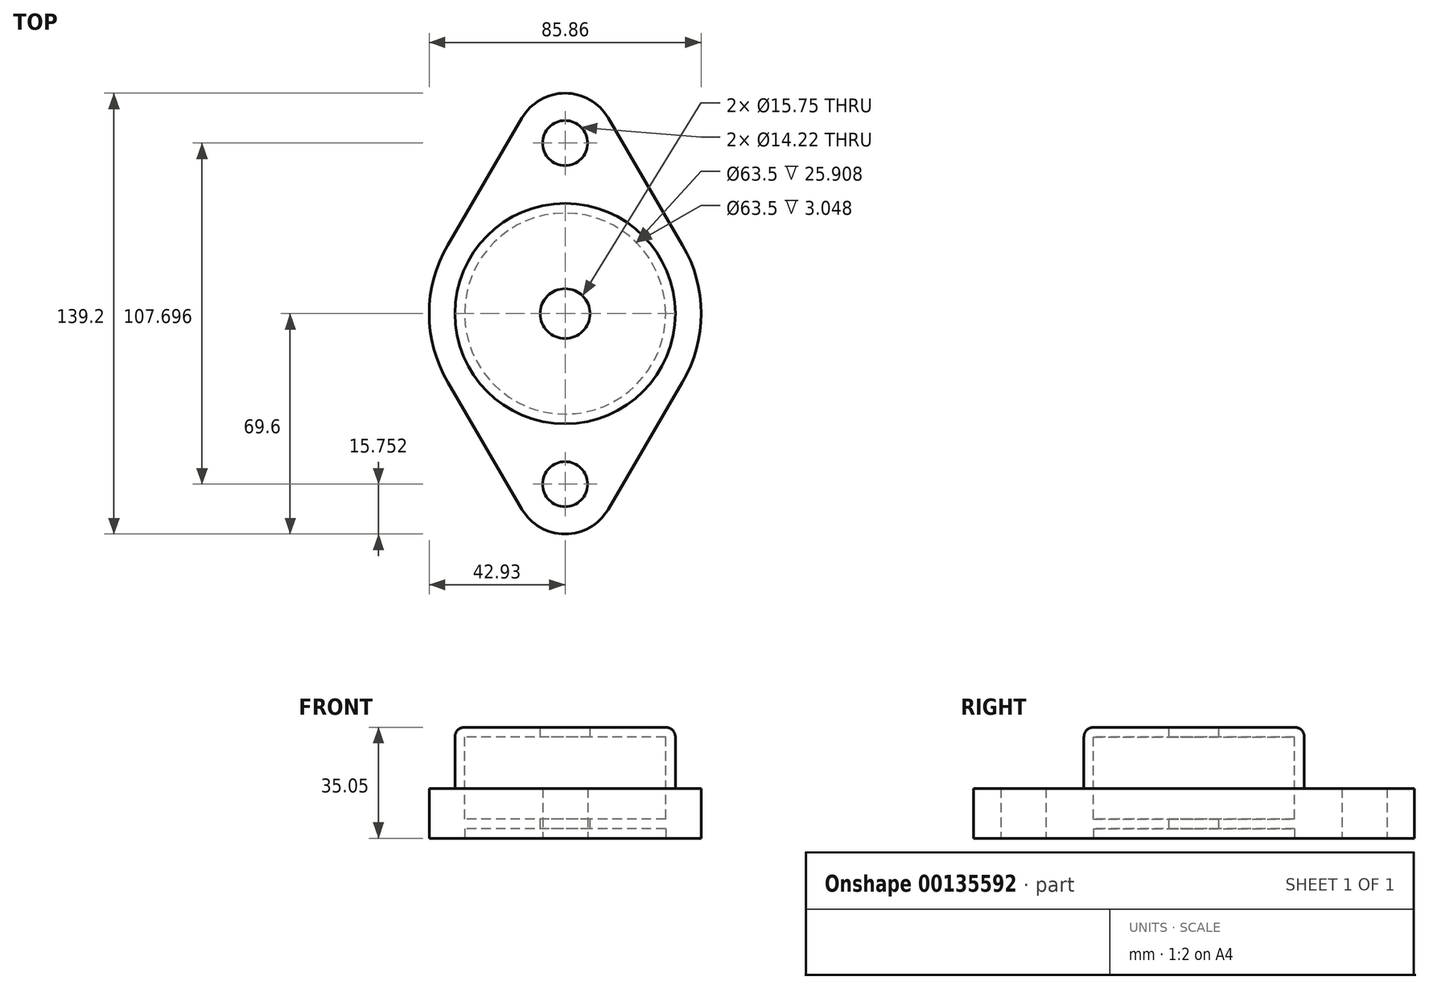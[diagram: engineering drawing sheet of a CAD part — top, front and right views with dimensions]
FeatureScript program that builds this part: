
annotation { "Feature Type Name" : "Feature", "Feature Type Description" : "" }
export const myFeature = defineFeature(function(context is Context, id is Id, definition is map)
    precondition{}
    {
        {
            var Q0;
            Q0=qCreatedBy(makeId("Front.planeOp"),FACE);
            var sketch = newSketch(context, id + "F0", { "sketchPlane" : qUnion([Q0])});
            skLineSegment(sketch, "E0", {"start": v(0, 89.64) * mm, "end": v(0, 0) * mm, "construction": true});
            skLineSegment(sketch, "E1", {"start": v(0, 38.1) * mm, "end": v(-7.87, 38.1) * mm});
            skLineSegment(sketch, "E2", {"start": v(-7.87, 38.1) * mm, "end": v(-7.87, 0) * mm});
            skLineSegment(sketch, "E3", {"start": v(-7.87, 0) * mm, "end": v(0, 0) * mm});
            skLineSegment(sketch, "E4", {"start": v(-7.87, 35.05) * mm, "end": v(-31.75, 35.05) * mm});
            skLineSegment(sketch, "E5", {"start": v(-34.8, 32) * mm, "end": v(-34.8, 6.1) * mm});
            skLineSegment(sketch, "E6", {"start": v(-31.75, 3.05) * mm, "end": v(0, 3.05) * mm});
            skArc(sketch, "E7", {"start": v(-31.75, 35.05) * mm, "mid": v(-33.9, 34.16) * mm, "end": v(-34.8, 32) * mm});
            skArc(sketch, "E8", {"start": v(-34.8, 6.1) * mm, "mid": v(-33.9, 3.94) * mm, "end": v(-31.75, 3.05) * mm});
            skLineSegment(sketch, "E9", {"start": v(-7.87, 32) * mm, "end": v(-31.75, 32) * mm});
            skLineSegment(sketch, "E10", {"start": v(-31.75, 32) * mm, "end": v(-31.75, 6.1) * mm});
            skLineSegment(sketch, "E11", {"start": v(-31.75, 6.1) * mm, "end": v(-7.87, 6.1) * mm});
            skSolve(sketch);
        }
        {
            var Q0;
            {var subQ0=sQuery(id+"F0.wireOp",EDGE,"E4");Q0=makeQuery(id+"F0.imprint","IMPRINT",FACE,{"disambiguationData":[TD([[makeQuery(id+"F0.imprint","IMPRINT",EDGE,{"derivedFrom":subQ0}),1.0]])]});}
            var Q1;
            Q1=sQuery(id+"F0.wireOp",EDGE,"E0");
            revolve(context, id + "F1", {"entities" : qUnion([Q0]), "axis" : qUnion([Q1]), "revolveType" : RevolveType.FULL});
        }
        {
            var Q0;
            Q0=qCreatedBy(makeId("Top.planeOp"),FACE);
            var sketch = newSketch(context, id + "F2", { "sketchPlane" : qUnion([Q0])});
            skLineSegment(sketch, "E12", {"start": v(0, 80.89) * mm, "end": v(0, -81.96) * mm, "construction": true});
            skCircle(sketch, "E13", {"center": v(0, 53.85) * mm, "radius": 7.11 * mm});
            skCircle(sketch, "E14", {"center": v(0, -53.85) * mm, "radius": 7.11 * mm});
            skArc(sketch, "E15", {"start": v(-13.6, -61.8) * mm, "mid": v(0, -69.6) * mm, "end": v(13.6, -61.8) * mm});
            skArc(sketch, "E16", {"start": v(13.6, 61.8) * mm, "mid": v(0, 69.6) * mm, "end": v(-13.6, 61.8) * mm});
            skLineSegment(sketch, "E17", {"start": v(-13.6, 61.8) * mm, "end": v(-37.06, 21.67) * mm});
            skLineSegment(sketch, "E18", {"start": v(-13.6, -61.8) * mm, "end": v(-37.06, -21.67) * mm});
            skLineSegment(sketch, "E19", {"start": v(13.6, 61.8) * mm, "end": v(37.06, 21.67) * mm});
            skLineSegment(sketch, "E20", {"start": v(13.6, -61.8) * mm, "end": v(37.06, -21.67) * mm});
            skArc(sketch, "E21", {"start": v(-37.06, 21.67) * mm, "mid": v(-42.93, 0) * mm, "end": v(-37.06, -21.67) * mm});
            skArc(sketch, "E22", {"start": v(37.06, -21.67) * mm, "mid": v(42.93, 0) * mm, "end": v(37.06, 21.67) * mm});
            skCircle(sketch, "E23.0", {"center": v(0, 0) * mm, "radius": 7.87 * mm});
            skCircle(sketch, "E24.0", {"center": v(0, 0) * mm, "radius": 31.75 * mm});
            skSolve(sketch);
        }
        {
            var Q0;
            Q0 = qSketchRegion(id + "F2", true);
            extrude(context, id + "F3", {"entities" : qUnion([Q0]), "operationType" : NewBodyOperationType.ADD, "depth" : 15.75 * mm});
        }
    });
